# Revit family: HydroTap_Assembled_Zip_Commercial_TouchFreeWave_CS
name_source: partatom
category: Plumbing Fixtures
units: mm (PartAtom-declared; Revit-internal decimal feet)

## family parameters
Always vertical = Yes
Cut with Voids When Loaded = Yes
OmniClass Number = 23.21.21.25
OmniClass Title = Commercial Food and Beverage Dispensing Equipment
Part Type = Normal
Room Calculation Point = No
Round Connector Dimension = Use Diameter
Shared = No
Work Plane-Based = No

## types (1)
- 100 People - Chrome (H5W765Z00AU)
    CW Connection = Yes
    ColdWaterOffset = 216 mm
    Description = Zip HydroTap Touch-Free Wave Chilled, Sparkling, Filtered water uses smart infrared 100% touch-free operation that is activated with the Wave of a hand. The water system features a single under bench command centre including full colour interactive touch screen display with pin code protection and customisable settings including 2 energy saving modes including ON/OFF timers and 2 hour sleep mode, 'Quiet' mode with automated intelligent fan speed adjustment, SteriTouch® antimicrobial protection impregnated into key water paths for enhanced hygiene, 100% water efficient air cooled technology, 0.2 micron water filtration, and a refillable CO2 cylinder. Easy to install integrated ventilation tray included.
    Electrical Connection = Yes
    ElectricalOffset = 108 mm
    FixtureMaterial = Metal_Chrome_Zip
    HW Connection = Yes
    IfcExportAs = IfcElectricAppliance
    IfcExportType = NOTDEFINED
    Manufacturer = Zip Australia
    ManufacturerOverallDepth = 476 mm  [stored 1.56168 ft]
    ManufacturerOverallHeight = 333 mm  [stored 1.09252 ft]
    ManufacturerOverallWidth = 280 mm  [stored 0.918635 ft]
    ManufacturerSpecCode = H5W765Z00AU
    ManufacturerURLProductSpecific = https://www.zipwater.com
    Model = 100 People - Chrome
    ModifiedIssue = 20230123 $
    Type Comments = HydroTap Wave CS - Chrome - 100 People
    URL = https://www.zipwater.com
    Uniclass2015Code = Pr_40_70_23_42
    Uniclass2015Title = Instant boiling and cold water taps
    Uniclass2015Version = Products v1.17
    Vent Connection = Yes

note: [stored X ft] marks values corroborated as IEEE doubles in the binary element streams (Revit-internal decimal feet)

## geometry (parser evidence)
native form markers: Sweep x12
no freeform markers — native parametric forms only
